# Revit family: FONESTAR_Altavoz_Colgante
name_source: partatom
category: Communication Devices
units: mm (PartAtom-declared; Revit-internal decimal feet)

## family parameters
Always vertical = No
Cut with Voids When Loaded = No
Maintain Annotation Orientation = No
Part Type = Normal
Room Calculation Point = No
Round Connector Dimension = Use Diameter
Shared = No
Work Plane-Based = Yes

## types (1)
- EF-333
    Cable.Diámetro = 10 mm  [stored 0.0328084 ft]
    Cable.Longitud = 400 mm  [stored 1.31234 ft]
    Cable.Material = Auxiliar - Blanco
    Cuerpo.Diámetro.Inferior = 100 mm  [stored 0.328084 ft]
    Cuerpo.Material = Plástico ABS - Blanco RAL(9002)
    Default Elevation = 1000 mm  [stored 3.28084 ft]
    Description = Altavoz colgante con transformador de línea 100 V y baja impedancia. Cobertura uniforme horizontal.
    Diámetro = 187 mm  [stored 0.613517 ft]
    Longitud = 245 mm  [stored 0.803806 ft]
    Manufacturer = FONESTAR
    Model = EF-333
    Modified by = XPV
    Peso = 2,1 Kg
    Potencia Acústica = 30 W RMS
    Protección IP = IP-54
    Rejilla.Curva.Espesor = 2 mm  [stored 0.00656168 ft]
    Rejilla.Espesor = 5 mm  [stored 0.0164042 ft]
    Rejilla.Material = Aluminio_Rejilla - Blanco RAL(9002)
    Remate.Altura = 50 mm  [stored 0.164042 ft]
    Remate.Diámetro.Inferior = 30 mm  [stored 0.0984252 ft]
    Remate.Díametro = 50 mm  [stored 0.164042 ft]
    Respuesta Acústica = 70-20.000 Hz
    Reviewed by = TAG
    Soporte.Material = Plástico ABS - Blanco RAL(9002)
    URL = https://fonestar.com
    URL.Product = https://fonestar.com
    Version = R0

note: [stored X ft] marks values corroborated as IEEE doubles in the binary element streams (Revit-internal decimal feet)
